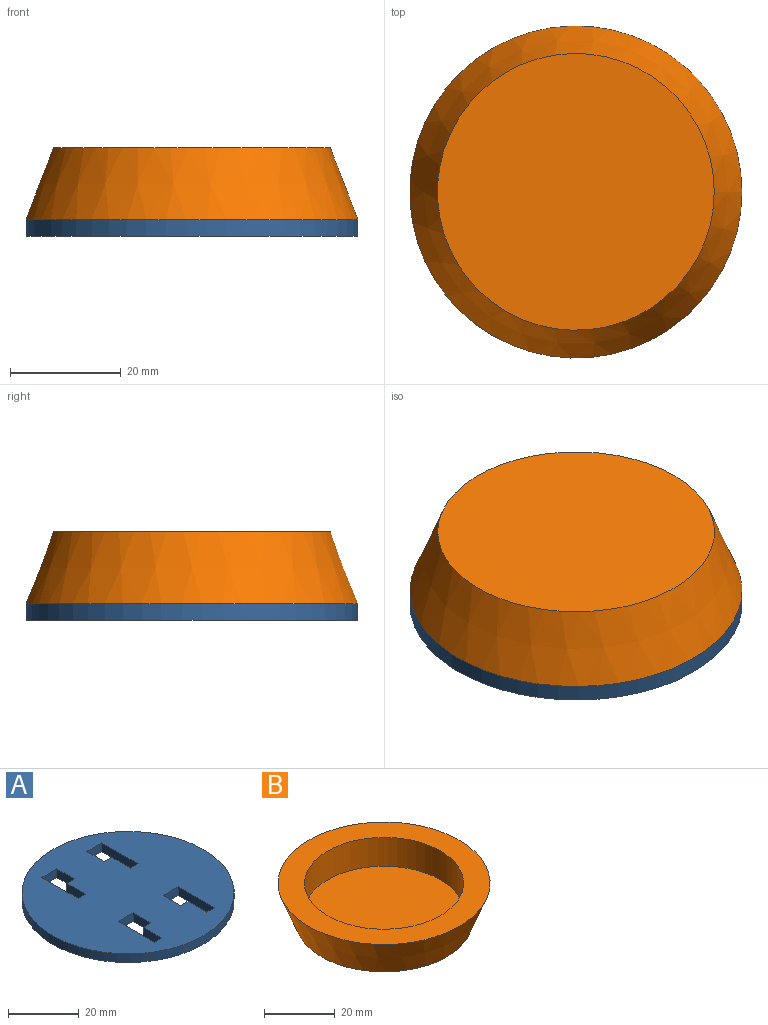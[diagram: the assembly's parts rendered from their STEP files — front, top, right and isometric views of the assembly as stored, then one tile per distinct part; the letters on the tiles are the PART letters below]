
ASSEMBLY  parts=2 mates=1
PART A: 27 faces, bbox 60x60x3 mm
  f0: plane 7x3mm, normal (1,0,0), area 21mm2, adj f1,f24,f25,f26
  f1: plane 6x3mm, normal (0,-1,0), area 18mm2, adj f0,f2,f25,f26
  f2: plane 14.5x3mm, normal (-1,0,0), area 43.5mm2, adj f1,f3,f25,f26
  f3: plane 3x3mm, normal (0,1,0), area 9mm2, adj f2,f4,f25,f26
  f4: plane 7.5x3mm, normal (1,0,0), area 22.5mm2, adj f3,f24,f25,f26
  f5: plane 6x3mm, normal (0,-1,0), area 18mm2, adj f6,f21,f25,f26
  f6: plane 7x3mm, normal (-1,0,0), area 21mm2, adj f5,f7,f25,f26
  f7: plane 3x3mm, normal (0,1,0), area 9mm2, adj f6,f8,f25,f26
  f8: plane 7.5x3mm, normal (-1,0,0), area 22.5mm2, adj f7,f9,f25,f26
  f9: plane 3x3mm, normal (0,1,0), area 9mm2, adj f8,f21,f25,f26
  f10: plane 3x3mm, normal (0,1,0), area 9mm2, adj f11,f22,f25,f26
  f11: plane 7.5x3mm, normal (1,0,0), area 22.5mm2, adj f10,f12,f25,f26
  f12: plane 3x3mm, normal (0,1,0), area 9mm2, adj f11,f13,f25,f26
  f13: plane 7x3mm, normal (1,0,0), area 21mm2, adj f12,f14,f25,f26
  f14: plane 6x3mm, normal (0,-1,0), area 18mm2, adj f13,f22,f25,f26
  f15: plane 7.5x3mm, normal (-1,0,0), area 22.5mm2, adj f16,f23,f25,f26
  f16: plane 3x3mm, normal (0,1,0), area 9mm2, adj f15,f17,f25,f26
  f17: plane 14.5x3mm, normal (1,0,0), area 43.5mm2, adj f16,f18,f25,f26
  f18: plane 6x3mm, normal (0,-1,0), area 18mm2, adj f17,f19,f25,f26
  f19: plane 7x3mm, normal (-1,0,0), area 21mm2, adj f18,f23,f25,f26
  f20: cylinder r=30mm len=60mm, axis (0,0,-1), area 565.5mm2, adj f25,f26
  f21: plane 14.5x3mm, normal (1,0,0), area 43.5mm2, adj f5,f9,f25,f26
  f22: plane 14.5x3mm, normal (-1,0,0), area 43.5mm2, adj f10,f14,f25,f26
  f23: plane 3x3mm, normal (0,1,0), area 9mm2, adj f15,f19,f25,f26
  f24: plane 3x3mm, normal (0,1,0), area 9mm2, adj f0,f4,f25,f26
  f25: plane 60x60mm, normal (0,0,1), area 2569.4mm2, adj f0,f1,f2,f3,f4,f5,f6,f7
  f26: plane 60x60mm, normal (0,0,-1), area 2569.4mm2, adj f0,f1,f2,f3,f4,f5,f6,f7
PART B: 5 faces, bbox 60x60x13 mm
  f0: cylinder r=22.5mm len=45mm, axis (0,0,-1), area 1413.7mm2, adj f1,f2
  f1: plane 60x60mm, normal (0,0,1), area 1237mm2, adj f0,f4
  f2: plane 45x45mm, normal (0,0,1), area 1590.4mm2, adj f0
  f3: plane 50x50mm, normal (0,0,-1), area 1963.5mm2, adj f4
  f4: cone r=30mm half-angle=21deg, axis (0,0,1), area 2406.7mm2, adj f1,f3
PLACE A t=(5.99,6.56,3.15)mm
PLACE B rot(axis=(1,0,0),180deg) t=(-45.61,66.22,16.15)mm
MATE fastened B.f0 <-> A.f20  axis (0,0,-1) through (5.99,6.56,6.15)mm
